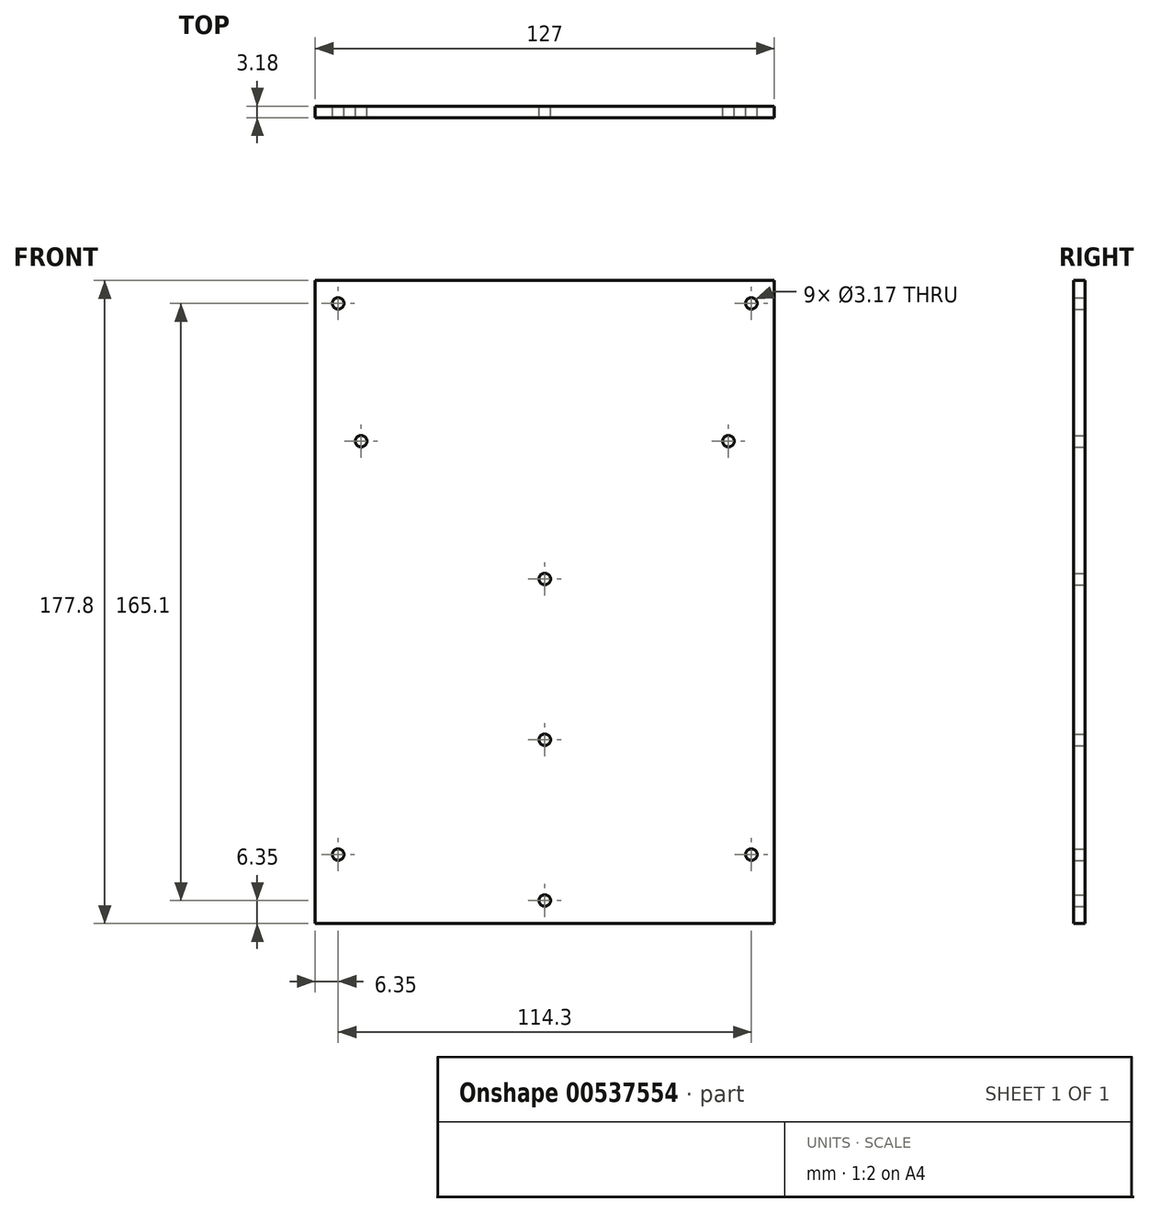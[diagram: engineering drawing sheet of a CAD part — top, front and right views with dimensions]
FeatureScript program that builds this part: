
annotation { "Feature Type Name" : "Feature", "Feature Type Description" : "" }
export const myFeature = defineFeature(function(context is Context, id is Id, definition is map)
    precondition{}
    {
        {
            var Q0;
            Q0=qCreatedBy(makeId("Front.planeOp"),FACE);
            var sketch = newSketch(context, id + "F0", { "sketchPlane" : qUnion([Q0])});
            skCircle(sketch, "E0", {"center": v(-63.5, 6.35) * mm, "radius": 12.7 * mm, "construction": true});
            skCircle(sketch, "E1", {"center": v(-63.5, 50.8) * mm, "radius": 31.75 * mm, "construction": true});
            skCircle(sketch, "E2", {"center": v(-63.5, 50.8) * mm, "radius": 12.7 * mm, "construction": true});
            skCircle(sketch, "E3", {"center": v(-63.5, 95.25) * mm, "radius": 31.75 * mm, "construction": true});
            skCircle(sketch, "E4", {"center": v(-63.5, 95.25) * mm, "radius": 1.59 * mm});
            skCircle(sketch, "E5", {"center": v(-63.5, 50.8) * mm, "radius": 1.59 * mm});
            skCircle(sketch, "E6", {"center": v(-63.5, 6.35) * mm, "radius": 1.59 * mm});
            skLineSegment(sketch, "E7.bottom", {"start": v(0, 0) * mm, "end": v(-127, 0) * mm});
            skLineSegment(sketch, "E7.top", {"start": v(0, 177.8) * mm, "end": v(-127, 177.8) * mm});
            skLineSegment(sketch, "E7.left", {"start": v(0, 0) * mm, "end": v(0, 177.8) * mm});
            skLineSegment(sketch, "E7.right", {"start": v(-127, 0) * mm, "end": v(-127, 177.8) * mm});
            skCircle(sketch, "E8", {"center": v(-6.35, 19.05) * mm, "radius": 1.59 * mm});
            skCircle(sketch, "E9", {"center": v(-6.35, 171.45) * mm, "radius": 1.59 * mm});
            skLineSegment(sketch, "E10", {"start": v(-63.5, 177.8) * mm, "end": v(-63.5, 0) * mm, "construction": true});
            skCircle(sketch, "E11.MirrorC", {"center": v(-120.65, 171.45) * mm, "radius": 1.59 * mm});
            skCircle(sketch, "E12.MirrorC", {"center": v(-120.65, 19.05) * mm, "radius": 1.59 * mm});
            skCircle(sketch, "E13", {"center": v(-114.3, 133.35) * mm, "radius": 31.75 * mm, "construction": true});
            skCircle(sketch, "E14", {"center": v(-12.7, 133.35) * mm, "radius": 31.75 * mm, "construction": true});
            skCircle(sketch, "E15", {"center": v(-12.7, 133.35) * mm, "radius": 1.59 * mm});
            skCircle(sketch, "E16", {"center": v(-114.3, 133.35) * mm, "radius": 1.59 * mm});
            skSolve(sketch);
        }
        {
            var Q0;
            Q0 = qSketchRegion(id + "F0", true);
            extrude(context, id + "F1", {"entities" : qUnion([Q0]), "depth" : 3.17 * mm, "offsetDistance" : 25.4 * mm});
        }
    });
